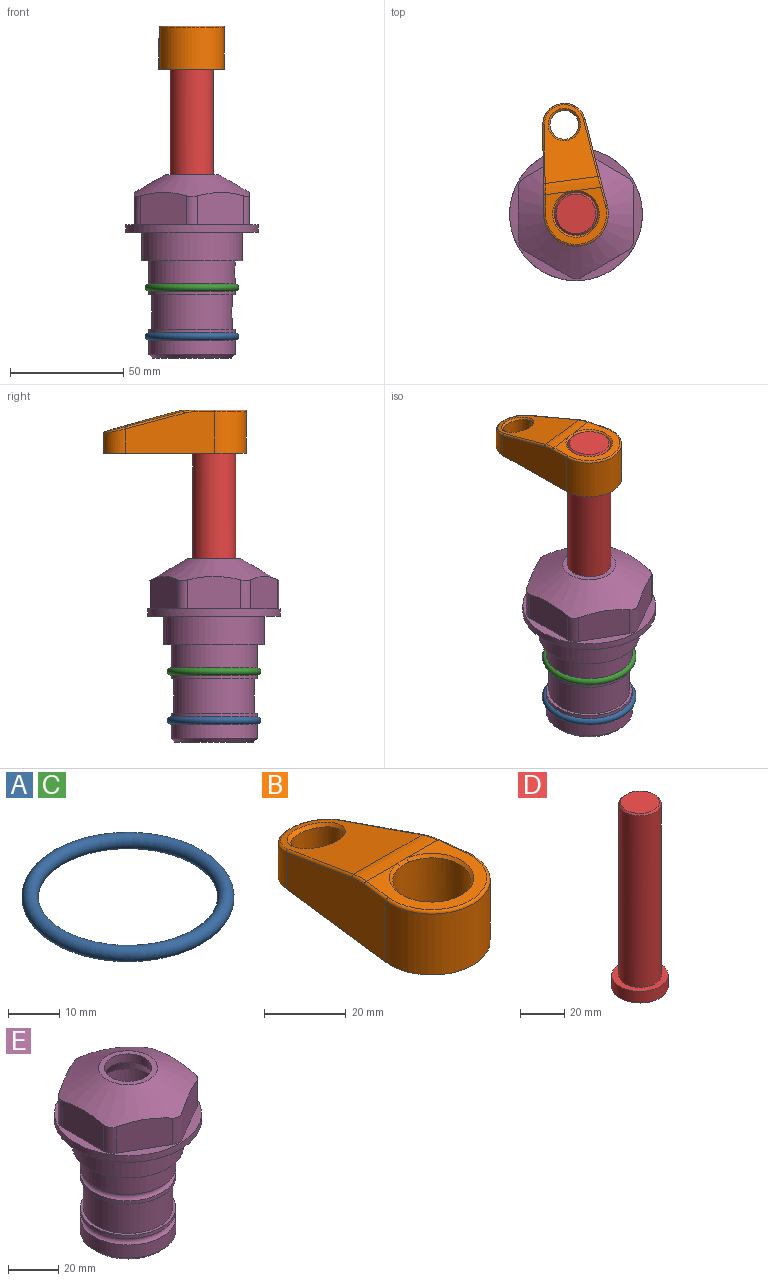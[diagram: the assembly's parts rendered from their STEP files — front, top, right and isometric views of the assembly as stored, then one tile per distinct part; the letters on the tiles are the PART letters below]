
ASSEMBLY  parts=5 mates=4
PART A: 1 faces, bbox 44.7x44.7x3.2 mm
  f0: torus R=19.05mm, axis (0,0,1), area 1193.9mm2
PART B: 31 faces, bbox 31.7x65.5x19.8 mm
  f0: plane 39.12x18.26mm, normal (0.99,0.12,0), area 612.2mm2, adj f1,f4,f7,f11,f13,f15
  f1: cylinder r=9.53mm len=18.91mm, axis (0,0,-1), area 296.1mm2, adj f0,f2,f7,f17
  f2: plane 39.12x18.26mm, normal (-0.99,0.12,0), area 612.2mm2, adj f1,f4,f7,f12,f14,f16
  f3: cylinder r=6.35mm len=12.7mm, axis (0,0,-1), area 362.4mm2, adj f7,f18
  f4: cylinder r=14.29mm len=28.58mm, axis (0,0,-1), area 882.2mm2, adj f0,f2,f7,f10
  f5: cylinder r=9.53mm len=19.05mm, axis (0,0,-1), area 1092.6mm2, adj f7,f19,f20
  f6: plane 26.99x23.69mm, normal (0,0,1), area 216.2mm2, adj f9,f10,f11,f12,f19
  f7: plane 63.5x28.58mm, normal (0,0,-1), area 661.8mm2, adj f0,f1,f2,f3,f4,f5,f22,f23
  f8: plane 33.52x23.6mm, normal (0,0.26,0.97), area 486mm2, adj f9,f15,f16,f17,f18
  f9: cylinder r=19.05mm len=24.72mm, axis (1,0,0), area 120.4mm2, adj f6,f8,f13,f14,f20
  f10: torus R=13.49mm, axis (0,0,1), area 59mm2, adj f4,f6,f11,f12
  f11: cylinder r=0.79mm len=8.67mm, axis (0.12,-0.99,0), area 10.8mm2, adj f0,f6,f10,f13
  f12: cylinder r=0.79mm len=8.67mm, axis (0.12,0.99,0), area 10.8mm2, adj f2,f6,f10,f14
  f13: bspline ~4.95x1.42mm, area 6.1mm2, adj f0,f9,f11,f15
  f14: bspline ~4.95x1.42mm, area 6.1mm2, adj f2,f9,f12,f16
  f15: cylinder r=0.79mm len=25.95mm, axis (0.12,-0.96,0.26), area 32.9mm2, adj f0,f8,f13,f17
  f16: cylinder r=0.79mm len=25.95mm, axis (0.12,0.96,-0.26), area 32.9mm2, adj f2,f8,f14,f17
  f17: bspline ~18.91x8.38mm, area 30mm2, adj f1,f8,f15,f16
  f18: bspline ~14.29x14.29mm, area 48.3mm2, adj f3,f8
  f19: cone r=9.53mm half-angle=45deg, axis (0,0,1), area 66.5mm2, adj f5,f6,f20
  f20: bspline ~3.22x0.96mm, area 3.5mm2, adj f5,f9,f19
  f21: plane 2.75x2.72mm, normal (0,0,-1), area 2.9mm2, adj f23,f25,f28
  f22: plane 23.05x15.88mm, normal (-0.99,-0.12,0), area 323.6mm2, adj f7,f25,f26,f27,f28,f29
  f23: plane 23.05x15.88mm, normal (0.99,-0.12,0), area 323.6mm2, adj f7,f21,f25,f27,f28,f30
  f24: cylinder r=9.53mm len=10.69mm, axis (0,0,-1), area 114.7mm2, adj f7,f27,f29,f30
  f25: cylinder r=12.7mm len=20.59mm, axis (0,0,-1), area 381.1mm2, adj f7,f21,f22,f23,f26,f28
  f26: plane 2.75x2.72mm, normal (0,0,-1), area 2.9mm2, adj f22,f25,f28
  f27: plane 19.72x18.37mm, normal (0,-0.26,-0.97), area 291.8mm2, adj f22,f23,f24,f28,f29,f30
  f28: cylinder r=15.88mm len=19.92mm, axis (1,0,0), area 54.8mm2, adj f21,f22,f23,f25,f26,f27
  f29: cylinder r=1.59mm len=11mm, axis (0,0,-1), area 34.7mm2, adj f7,f22,f24,f27
  f30: cylinder r=1.59mm len=11mm, axis (0,0,-1), area 34.7mm2, adj f7,f23,f24,f27
PART C: same geometry as A
PART D: 6 faces, bbox 25.4x25.4x101.6 mm
  f0: plane 17.46x17.46mm, normal (0,0,1), area 239.5mm2, adj f5
  f1: plane 25.4x25.4mm, normal (0,0,-1), area 506.7mm2, adj f2
  f2: cylinder r=12.7mm len=25.4mm, axis (0,0,1), area 506.7mm2, adj f1,f3
  f3: plane 25.4x25.4mm, normal (0,0,1), area 221.7mm2, adj f2,f4
  f4: cylinder r=9.53mm len=94.46mm, axis (0,0,1), area 5653mm2, adj f3,f5
  f5: cone r=8.73mm half-angle=45deg, axis (0,0,-1), area 64.4mm2, adj f0,f4
PART E: 36 faces, bbox 58.7x58.7x81 mm
  f0: cylinder r=17.78mm len=35.56mm, axis (0,0,1), area 1670.8mm2, adj f23,f24,f31
  f1: cylinder r=19.05mm len=38.1mm, axis (0,0,1), area 1191.9mm2, adj f26,f27,f30
  f2: plane 58.66x58.66mm, normal (0,0,-1), area 1150.6mm2, adj f3,f28
  f3: cylinder r=29.33mm len=58.66mm, axis (0,0,-1), area 585.1mm2, adj f2,f4
  f4: plane 58.66x58.66mm, normal (0,0,1), area 475.9mm2, adj f3,f5,f6,f7,f8,f9,f10,f11
  f5: plane 20.32x14.34mm, normal (-0.5,0.87,0), area 324.4mm2, adj f4,f15,f16,f17
  f6: plane 20.32x14.34mm, normal (0.5,0.87,0), area 324.4mm2, adj f4,f14,f15,f17
  f7: plane 23.48x14.34mm, normal (1,0,0), area 324.4mm2, adj f4,f13,f14,f17
  f8: plane 20.32x14.34mm, normal (0.5,-0.87,0), area 324.4mm2, adj f4,f12,f13,f17
  f9: plane 20.32x14.34mm, normal (-0.5,-0.87,0), area 324.4mm2, adj f4,f11,f12,f17
  f10: plane 23.48x14.34mm, normal (-1,0,0), area 324.4mm2, adj f4,f11,f16,f17
  f11: cylinder r=5.08mm len=12.85mm, axis (0,0,-1), area 67.2mm2, adj f4,f9,f10,f17
  f12: cylinder r=5.08mm len=12.85mm, axis (0,0,-1), area 67.2mm2, adj f4,f8,f9,f17
  f13: cylinder r=5.08mm len=12.85mm, axis (0,0,-1), area 67.2mm2, adj f4,f7,f8,f17
  f14: cylinder r=5.08mm len=12.85mm, axis (0,0,-1), area 67.2mm2, adj f4,f6,f7,f17
  f15: cylinder r=5.08mm len=12.85mm, axis (0,0,-1), area 67.2mm2, adj f4,f5,f6,f17
  f16: cylinder r=5.08mm len=12.85mm, axis (0,0,-1), area 67.2mm2, adj f4,f5,f10,f17
  f17: cone r=11.73mm half-angle=60deg, axis (0,0,-1), area 2071.8mm2, adj f5,f6,f7,f8,f9,f10,f11,f12
  f18: plane 23.46x23.46mm, normal (0,0,1), area 147.4mm2, adj f17,f35
  f19: plane 34.93x34.93mm, normal (0,0,-1), area 958mm2, adj f29
  f20: cylinder r=19.05mm len=38.1mm, axis (0,0,1), area 760.1mm2, adj f21,f29
  f21: torus R=19.05mm, axis (0,0,1), area 565.3mm2, adj f20,f22
  f22: cylinder r=19.05mm len=38.1mm, axis (0,0,1), area 190mm2, adj f21,f23
  f23: plane 38.1x38.1mm, normal (0,0,1), area 146.9mm2, adj f0,f22
  f24: plane 38.1x38.1mm, normal (0,0,-1), area 146.9mm2, adj f0,f25
  f25: cylinder r=19.05mm len=38.1mm, axis (0,0,1), area 190mm2, adj f24,f26
  f26: torus R=19.05mm, axis (0,0,1), area 565.3mm2, adj f1,f25
  f27: plane 44.45x44.45mm, normal (0,0,-1), area 411.7mm2, adj f1,f28
  f28: cylinder r=22.23mm len=44.45mm, axis (0,0,1), area 1773.5mm2, adj f2,f27
  f29: cone r=19.05mm half-angle=45deg, axis (0,0,1), area 257.5mm2, adj f19,f20
  f30: cylinder r=3.17mm len=6.75mm, axis (-1,0,0), area 128mm2, adj f1,f33
  f31: cylinder r=3.17mm len=6.35mm, axis (-1,0,0), area 102.5mm2, adj f0,f33
  f32: plane 25.4x25.4mm, normal (0,0,1), area 506.7mm2, adj f33
  f33: cylinder r=12.7mm len=66.42mm, axis (0,0,-1), area 5236.2mm2, adj f30,f31,f32,f34
  f34: cone r=9.53mm half-angle=30deg, axis (0,0,-1), area 443.4mm2, adj f33,f35
  f35: cylinder r=9.53mm len=19.05mm, axis (0,0,-1), area 240.9mm2, adj f18,f34
PLACE A t=(0,0,-21.59)mm
PLACE B rot(axis=(0,0,1),7.5deg) t=(0,0,27.55)mm
PLACE C at identity
PLACE D rot(axis=(0,0,-1),172.5deg) t=(0,0,27.55)mm
PLACE E at identity fixed
MATE fastened A.f0 <-> E.f0  axis (0,0,1) through (0,0,-46.1)mm
MATE cylindrical D.f2 <-> E.f0  axis (0,0,-1) through (0,0,-10.55)mm
MATE fastened D.f2 <-> B.f4  axis (0,0,1) through (0,0,91.05)mm
MATE fastened E.f0 <-> C.f0  axis (0,0,1) through (0,0,-24.51)mm
